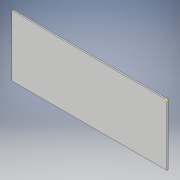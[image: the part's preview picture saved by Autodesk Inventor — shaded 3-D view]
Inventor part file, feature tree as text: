
AUTODESK INVENTOR PART (.ipt)
format: ipt  version: 2018 (Build 220112000, 112)  size: 96,256 bytes
history: native  units: mm
features: sketch x2, extrude x1
ambient origin geometry x8: Origin, YZ Plane, XZ Plane, XY Plane, X Axis, Y Axis, Z Axis, Center Point
bodies: Volumenkörper1 (feature_tree)
feature tree (3):
  sketch  "Skizze1"  dims[d0=165.0mm d1=65.0mm]
  extrude  "Extrusion1"  Depth=65.0mm
  sketch  "Skizze2"  dims[d2=1.5mm d3=0.0mm]
